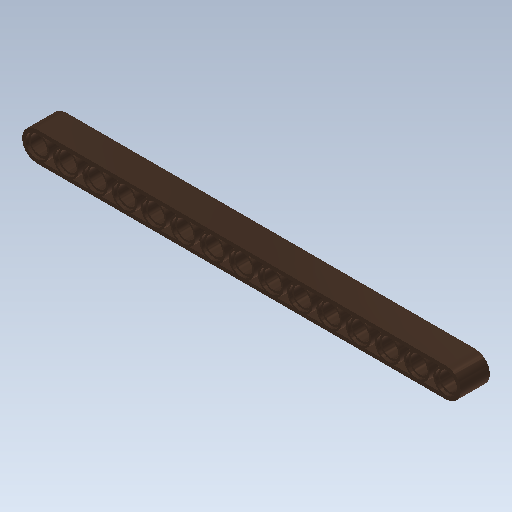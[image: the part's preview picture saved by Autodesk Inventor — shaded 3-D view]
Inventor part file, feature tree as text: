
AUTODESK INVENTOR PART (.ipt)
format: ipt  version: 2020 (Build 240168000, 168)  size: 333,312 bytes
history: native  units: mm
features: extrude x5, sketch x5
ambient origin geometry x8: Origin, YZ Plane, XZ Plane, XY Plane, X Axis, Y Axis, Z Axis, Center Point
bodies: Solid1 (feature_tree)
feature tree (10):
  extrude  "Extrusion1"  Depth=4.0mm
  extrude  "Extrusion26"  TaperAngle=0.0deg  [1 undecoded]
  extrude  "Extrusion27"  TaperAngle=180.0deg  [1 undecoded]
  extrude  "Extrusion28"  Depth=8.0mm TaperAngle=0.0deg
  extrude  "Extrusion29"  Depth=0.8mm
  sketch  "Sketch2"  dims[d0=4.0mm d1=4.0mm]
  sketch  "Sketch27"  dims[d2=112.0mm d3=0.0mm]
  sketch  "Sketch28"  dims[d4=56.0mm d9=180.0deg]
  sketch  "Sketch29"  dims[d10=0.0mm d12=8.0mm d13=0.0mm]
  sketch  "Sketch30"  dims[d268=112.0mm d269=5.0mm d270=10.0mm d272=10.0mm d273=150.0mm d275=8.0mm d277=10.0mm d278=0.0mm d279=6.0mm d280=10.0mm d282=10.0mm d283=150.0mm d285=8.0mm d287=0.8mm d288=0.0mm d289=6.0mm d290=10.0mm d292=10.0mm d293=150.0mm d295=8.0mm d297=0.8mm d298=0.0mm d299=7.0mm d300=7.0mm d301=10.0mm d303=10.0mm d304=140.0mm d306=8.0mm d308=0.8mm d309=0.0mm]
note: 2 required parameter values undecoded (feature->parameter linkage not recoverable at this tier; creation-order binding heuristic only, values carry confidence <= 0.55)
